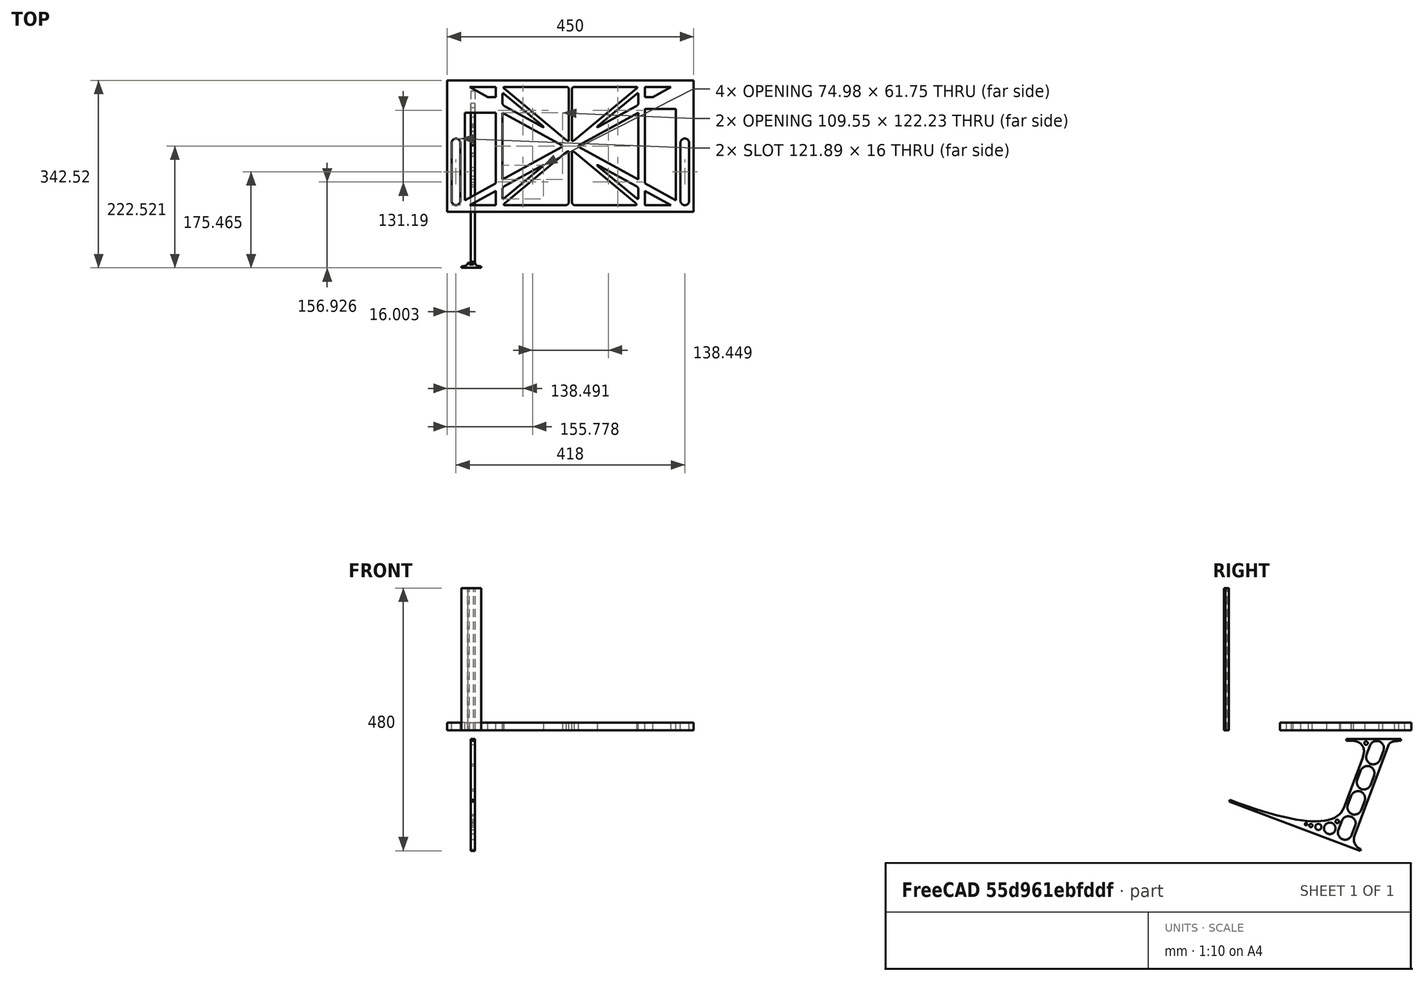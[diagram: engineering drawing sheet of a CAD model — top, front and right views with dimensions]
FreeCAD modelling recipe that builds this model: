
FCSTD DOCUMENT  (FreeCAD 0.19R0.19.2)
Label: laptopStand085
License: All rights reserved
LicenseURL: http://en.wikipedia.org/wiki/All_rights_reserved
objects: Sketcher::SketchObject×3, Part::Extrusion×3
note: 6 computed .brp shape members not serialized (recipe doc carries the construction recipe); baked Part::Feature solids carry a one-line shape summary decoded from their .brp

FEATURE [Sketcher::SketchObject] Sketch
  FullyConstrained = true
  sketch-geometry (220):
    g0: LineSegment StartX=-10.9272 StartY=-82.7794 StartZ=0 EndX=46.0728 EndY=-51.4823 EndZ=0
    g1: LineSegment StartX=366.073 StartY=-91.7794 StartZ=0 EndX=318.073 EndY=-65.424 EndZ=0
    g2: LineSegment StartX=-10.9272 StartY=77.3346 StartZ=0 EndX=-10.9272 EndY=-82.7794 EndZ=0
    g3: LineSegment StartX=375.073 StartY=-82.7794 StartZ=0 EndX=375.073 EndY=83.9235 EndZ=0
    g4: LineSegment StartX=-1.92719 StartY=-91.7794 StartZ=0 EndX=46.0728 EndY=-91.7794 EndZ=0
    g5: LineSegment StartX=318.073 StartY=124.221 StartZ=0 EndX=366.073 EndY=124.221 EndZ=0
    g6: LineSegment StartX=306.073 StartY=77.3346 StartZ=0 EndX=306.073 EndY=-44.8935 EndZ=0
    g7: LineSegment StartX=318.073 StartY=83.9235 StartZ=0 EndX=318.073 EndY=-51.4823 EndZ=0
    g8: LineSegment StartX=318.073 StartY=-51.4823 StartZ=0 EndX=375.073 EndY=-82.7794 EndZ=0
    g9: LineSegment StartX=318.073 StartY=-65.424 StartZ=0 EndX=318.073 EndY=-91.7794 EndZ=0
    g10: LineSegment StartX=318.073 StartY=-91.7794 StartZ=0 EndX=366.073 EndY=-91.7794 EndZ=0
    g11: LineSegment StartX=58.0728 StartY=-44.8935 StartZ=0 EndX=58.0728 EndY=77.3346 EndZ=0
    g12: LineSegment StartX=46.0728 StartY=-65.424 StartZ=0 EndX=-1.92719 EndY=-91.7794 EndZ=0
    g13: LineSegment StartX=46.0728 StartY=-65.424 StartZ=0 EndX=46.0728 EndY=-91.7794 EndZ=0
    g14: LineSegment StartX=46.0728 StartY=77.3346 StartZ=0 EndX=46.0728 EndY=-51.4823 EndZ=0
    g15: LineSegment StartX=-42.9272 StartY=136.221 StartZ=0 EndX=-42.9272 EndY=-103.779 EndZ=0
    g16: LineSegment StartX=407.073 StartY=136.221 StartZ=0 EndX=407.073 EndY=-103.779 EndZ=0
    g17: ArcOfCircle CenterX=-26.9272 CenterY=22.1087 CenterZ=0 NormalX=0 NormalY=0 NormalZ=1 AngleXU=0 Radius=8 StartAngle=1e-16 EndAngle=3.14159
    g18: ArcOfCircle CenterX=-26.9272 CenterY=-83.7794 CenterZ=0 NormalX=0 NormalY=0 NormalZ=1 AngleXU=0 Radius=8 StartAngle=3.14159 EndAngle=6.28319
    g19: LineSegment StartX=-34.9272 StartY=22.1087 StartZ=0 EndX=-34.9272 EndY=-83.7794 EndZ=0
    g20: LineSegment StartX=-18.9272 StartY=22.1087 StartZ=0 EndX=-18.9272 EndY=-83.7794 EndZ=0
    g21: ArcOfCircle CenterX=391.073 CenterY=22.1087 CenterZ=0 NormalX=0 NormalY=0 NormalZ=1 AngleXU=0 Radius=8 StartAngle=-4.4e-15 EndAngle=3.14159
    g22: LineSegment StartX=399.073 StartY=22.1087 StartZ=0 EndX=399.073 EndY=-83.7794 EndZ=0
    g23: LineSegment StartX=383.073 StartY=22.1087 StartZ=0 EndX=383.073 EndY=-83.7794 EndZ=0
    g24: ArcOfCircle CenterX=391.073 CenterY=-83.7794 CenterZ=0 NormalX=0 NormalY=0 NormalZ=1 AngleXU=0 Radius=8 StartAngle=3.14159 EndAngle=6.28319
    g25: Circle CenterX=175.022 CenterY=27.0628 CenterZ=0 NormalX=0 NormalY=0 NormalZ=1 AngleXU=0 Radius=1
    g26: Circle CenterX=179.022 CenterY=24.8665 CenterZ=0 NormalX=0 NormalY=0 NormalZ=1 AngleXU=0 Radius=1
    g27: Circle CenterX=179.022 CenterY=27.0628 CenterZ=0 NormalX=0 NormalY=0 NormalZ=1 AngleXU=0 Radius=1
    g28: BSplineCurve PolesCount=3 KnotsCount=2 Degree=2 IsPeriodic=0
    g29: GeomPoint X=175.022 Y=27.0628 Z=0
    g30: GeomPoint X=179.022 Y=27.0628 Z=0
    g31: Circle CenterX=189.124 CenterY=27.0628 CenterZ=0 NormalX=0 NormalY=0 NormalZ=1 AngleXU=0 Radius=1
    g32: Circle CenterX=185.124 CenterY=24.8665 CenterZ=0 NormalX=0 NormalY=0 NormalZ=1 AngleXU=0 Radius=1
    g33: Circle CenterX=185.124 CenterY=27.0628 CenterZ=0 NormalX=0 NormalY=0 NormalZ=1 AngleXU=0 Radius=1
    g34: BSplineCurve PolesCount=3 KnotsCount=2 Degree=2 IsPeriodic=0
    g35: GeomPoint X=189.124 Y=27.0628 Z=0
    g36: GeomPoint X=185.124 Y=27.0628 Z=0
    g37: Circle CenterX=175.022 CenterY=5.37834 CenterZ=0 NormalX=0 NormalY=0 NormalZ=1 AngleXU=0 Radius=1
    g38: Circle CenterX=179.022 CenterY=7.57463 CenterZ=0 NormalX=0 NormalY=0 NormalZ=1 AngleXU=0 Radius=1
    g39: Circle CenterX=179.022 CenterY=5.34704 CenterZ=0 NormalX=0 NormalY=0 NormalZ=1 AngleXU=0 Radius=1
    g40: BSplineCurve PolesCount=3 KnotsCount=2 Degree=2 IsPeriodic=0
    g41: GeomPoint X=175.022 Y=5.37834 Z=0
    g42: GeomPoint X=179.022 Y=5.34704 Z=0
    g43: Circle CenterX=189.124 CenterY=5.37834 CenterZ=0 NormalX=0 NormalY=0 NormalZ=1 AngleXU=0 Radius=1
    g44: Circle CenterX=185.124 CenterY=7.57463 CenterZ=0 NormalX=0 NormalY=0 NormalZ=1 AngleXU=0 Radius=1
    g45: Circle CenterX=185.124 CenterY=5.34704 CenterZ=0 NormalX=0 NormalY=0 NormalZ=1 AngleXU=0 Radius=1
    g46: BSplineCurve PolesCount=3 KnotsCount=2 Degree=2 IsPeriodic=0
    g47: GeomPoint X=189.124 Y=5.37834 Z=0
    g48: GeomPoint X=185.124 Y=5.34704 Z=0
    g49: Circle CenterX=165.871 CenterY=18.1458 CenterZ=0 NormalX=0 NormalY=0 NormalZ=1 AngleXU=0 Radius=1
    g50: Circle CenterX=169.377 CenterY=16.2206 CenterZ=0 NormalX=0 NormalY=0 NormalZ=1 AngleXU=0 Radius=1
    g51: Circle CenterX=165.871 CenterY=14.2954 CenterZ=0 NormalX=0 NormalY=0 NormalZ=1 AngleXU=0 Radius=1
    g52: BSplineCurve PolesCount=3 KnotsCount=2 Degree=2 IsPeriodic=0
    g53: GeomPoint X=165.871 Y=18.1458 Z=0
    g54: GeomPoint X=165.871 Y=14.2954 Z=0
    g55: Circle CenterX=198.275 CenterY=18.1458 CenterZ=0 NormalX=0 NormalY=0 NormalZ=1 AngleXU=0 Radius=1
    g56: Circle CenterX=194.768 CenterY=16.2206 CenterZ=0 NormalX=0 NormalY=0 NormalZ=1 AngleXU=0 Radius=1
    g57: Circle CenterX=198.275 CenterY=14.2954 CenterZ=0 NormalX=0 NormalY=0 NormalZ=1 AngleXU=0 Radius=1
    g58: BSplineCurve PolesCount=3 KnotsCount=2 Degree=2 IsPeriodic=0
    g59: GeomPoint X=198.275 Y=18.1458 Z=0
    g60: GeomPoint X=198.275 Y=14.2954 Z=0
    g61: LineSegment StartX=165.871 StartY=18.1458 StartZ=0 EndX=58.0728 EndY=77.3346 EndZ=0
    g62: LineSegment StartX=58.0728 StartY=-44.8935 StartZ=0 EndX=165.871 EndY=14.2954 EndZ=0
    g63: LineSegment StartX=198.275 StartY=18.1458 StartZ=0 EndX=306.073 EndY=77.3346 EndZ=0
    g64: LineSegment StartX=198.275 StartY=14.2954 StartZ=0 EndX=306.073 EndY=-44.8935 EndZ=0
    g65: LineSegment StartX=407.073 StartY=-103.779 StartZ=0 EndX=-42.9272 EndY=-103.779 EndZ=0
    g66: LineSegment StartX=407.073 StartY=136.221 StartZ=0 EndX=-42.9272 EndY=136.221 EndZ=0
    g67: LineSegment StartX=46.0728 StartY=77.3346 StartZ=0 EndX=-10.9272 EndY=77.3346 EndZ=0
    g68: LineSegment StartX=46.0728 StartY=105.865 StartZ=0 EndX=31.5028 EndY=105.865 EndZ=0
    g69: LineSegment StartX=46.0728 StartY=124.221 StartZ=0 EndX=46.0728 EndY=105.865 EndZ=0
    g70: LineSegment StartX=-1.92719 StartY=124.221 StartZ=0 EndX=31.5028 EndY=105.865 EndZ=0
    g71: LineSegment StartX=46.0728 StartY=124.221 StartZ=0 EndX=-1.92719 EndY=124.221 EndZ=0
    g72: LineSegment StartX=318.073 StartY=83.9235 StartZ=0 EndX=375.073 EndY=83.9235 EndZ=0
    g73: LineSegment StartX=318.073 StartY=105.865 StartZ=0 EndX=332.643 EndY=105.865 EndZ=0
    g74: LineSegment StartX=332.643 StartY=105.865 StartZ=0 EndX=366.073 EndY=124.221 EndZ=0
    g75: LineSegment StartX=318.073 StartY=124.221 StartZ=0 EndX=318.073 EndY=105.865 EndZ=0
    g76: Circle CenterX=125.607 CenterY=54.1951 CenterZ=0 NormalX=0 NormalY=0 NormalZ=1 AngleXU=0 Radius=1
    g77: Circle CenterX=139.632 CenterY=46.4944 CenterZ=0 NormalX=0 NormalY=0 NormalZ=1 AngleXU=0 Radius=1
    g78: Circle CenterX=127.326 CenterY=56.7187 CenterZ=0 NormalX=0 NormalY=0 NormalZ=1 AngleXU=0 Radius=1
    g79: BSplineCurve PolesCount=3 KnotsCount=2 Degree=2 IsPeriodic=0
    g80: GeomPoint X=125.607 Y=54.1951 Z=0
    g81: GeomPoint X=127.326 Y=56.7187 Z=0
    g82: Circle CenterX=236.821 CenterY=56.7187 CenterZ=0 NormalX=0 NormalY=0 NormalZ=1 AngleXU=0 Radius=1
    g83: Circle CenterX=224.513 CenterY=46.4944 CenterZ=0 NormalX=0 NormalY=0 NormalZ=1 AngleXU=0 Radius=1
    g84: Circle CenterX=238.538 CenterY=54.1951 CenterZ=0 NormalX=0 NormalY=0 NormalZ=1 AngleXU=0 Radius=1
    g85: BSplineCurve PolesCount=3 KnotsCount=2 Degree=2 IsPeriodic=0
    g86: GeomPoint X=236.821 Y=56.7187 Z=0
    g87: GeomPoint X=238.538 Y=54.1951 Z=0
    g88: Circle CenterX=238.538 CenterY=-21.7539 CenterZ=0 NormalX=0 NormalY=0 NormalZ=1 AngleXU=0 Radius=1
    g89: Circle CenterX=224.513 CenterY=-14.0532 CenterZ=0 NormalX=0 NormalY=0 NormalZ=1 AngleXU=0 Radius=1
    g90: Circle CenterX=236.821 CenterY=-24.2775 CenterZ=0 NormalX=0 NormalY=0 NormalZ=1 AngleXU=0 Radius=1
    g91: BSplineCurve PolesCount=3 KnotsCount=2 Degree=2 IsPeriodic=0
    g92: GeomPoint X=238.538 Y=-21.7539 Z=0
    g93: GeomPoint X=236.821 Y=-24.2775 Z=0
    g94: Circle CenterX=125.607 CenterY=-21.7539 CenterZ=0 NormalX=0 NormalY=0 NormalZ=1 AngleXU=0 Radius=1
    g95: Circle CenterX=139.632 CenterY=-14.0532 CenterZ=0 NormalX=0 NormalY=0 NormalZ=1 AngleXU=0 Radius=1
    g96: Circle CenterX=127.325 CenterY=-24.2775 CenterZ=0 NormalX=0 NormalY=0 NormalZ=1 AngleXU=0 Radius=1
    g97: BSplineCurve PolesCount=3 KnotsCount=2 Degree=2 IsPeriodic=0
    g98: GeomPoint X=125.607 Y=-21.7539 Z=0
    g99: GeomPoint X=127.325 Y=-24.2775 Z=0
    g100: Circle CenterX=302.996 CenterY=111.695 CenterZ=0 NormalX=0 NormalY=0 NormalZ=1 AngleXU=0 Radius=1
    g101: Circle CenterX=306.073 CenterY=114.251 CenterZ=0 NormalX=0 NormalY=0 NormalZ=1 AngleXU=0 Radius=1
    g102: Circle CenterX=306.073 CenterY=110.251 CenterZ=0 NormalX=0 NormalY=0 NormalZ=1 AngleXU=0 Radius=1
    g103: BSplineCurve PolesCount=3 KnotsCount=2 Degree=2 IsPeriodic=0
    g104: GeomPoint X=302.996 Y=111.695 Z=0
    g105: GeomPoint X=306.073 Y=110.251 Z=0
    g106: Circle CenterX=306.073 CenterY=95.2763 CenterZ=0 NormalX=0 NormalY=0 NormalZ=1 AngleXU=0 Radius=1
    g107: Circle CenterX=306.073 CenterY=91.2763 CenterZ=0 NormalX=0 NormalY=0 NormalZ=1 AngleXU=0 Radius=1
    g108: Circle CenterX=302.567 CenterY=89.3511 CenterZ=0 NormalX=0 NormalY=0 NormalZ=1 AngleXU=0 Radius=1
    g109: BSplineCurve PolesCount=3 KnotsCount=2 Degree=2 IsPeriodic=0
    g110: GeomPoint X=306.073 Y=95.2763 Z=0
    g111: GeomPoint X=302.567 Y=89.3511 Z=0
    g112: LineSegment StartX=306.073 StartY=110.251 StartZ=0 EndX=306.073 EndY=95.2763 EndZ=0
    g113: LineSegment StartX=302.996 StartY=111.695 StartZ=0 EndX=236.821 EndY=56.7187 EndZ=0
    g114: LineSegment StartX=238.538 StartY=54.1951 StartZ=0 EndX=302.567 EndY=89.3511 EndZ=0
    g115: Circle CenterX=61.1496 CenterY=111.695 CenterZ=0 NormalX=0 NormalY=0 NormalZ=1 AngleXU=0 Radius=1
    g116: Circle CenterX=58.0728 CenterY=114.251 CenterZ=0 NormalX=0 NormalY=0 NormalZ=1 AngleXU=0 Radius=1
    g117: Circle CenterX=58.0728 CenterY=110.251 CenterZ=0 NormalX=0 NormalY=0 NormalZ=1 AngleXU=0 Radius=1
    g118: BSplineCurve PolesCount=3 KnotsCount=2 Degree=2 IsPeriodic=0
    g119: GeomPoint X=61.1496 Y=111.695 Z=0
    g120: GeomPoint X=58.0728 Y=110.251 Z=0
    g121: Circle CenterX=61.5791 CenterY=89.3511 CenterZ=0 NormalX=0 NormalY=0 NormalZ=1 AngleXU=0 Radius=1
    g122: Circle CenterX=58.0728 CenterY=91.2763 CenterZ=0 NormalX=0 NormalY=0 NormalZ=1 AngleXU=0 Radius=1
    g123: Circle CenterX=58.0728 CenterY=95.2763 CenterZ=0 NormalX=0 NormalY=0 NormalZ=1 AngleXU=0 Radius=1
    g124: BSplineCurve PolesCount=3 KnotsCount=2 Degree=2 IsPeriodic=0
    g125: GeomPoint X=61.5791 Y=89.3511 Z=0
    g126: GeomPoint X=58.0728 Y=95.2763 Z=0
    g127: LineSegment StartX=58.0728 StartY=110.251 StartZ=0 EndX=58.0728 EndY=95.2763 EndZ=0
    g128: LineSegment StartX=61.1496 StartY=111.695 StartZ=0 EndX=127.326 EndY=56.7187 EndZ=0
    g129: LineSegment StartX=125.607 StartY=54.1951 StartZ=0 EndX=61.5791 EndY=89.3511 EndZ=0
    g130: Circle CenterX=61.5791 CenterY=-56.9099 CenterZ=0 NormalX=0 NormalY=0 NormalZ=1 AngleXU=0 Radius=1
    g131: Circle CenterX=58.0728 CenterY=-58.8351 CenterZ=0 NormalX=0 NormalY=0 NormalZ=1 AngleXU=0 Radius=1
    g132: Circle CenterX=58.0728 CenterY=-62.8351 CenterZ=0 NormalX=0 NormalY=0 NormalZ=1 AngleXU=0 Radius=1
    g133: BSplineCurve PolesCount=3 KnotsCount=2 Degree=2 IsPeriodic=0
    g134: GeomPoint X=61.5791 Y=-56.9099 Z=0
    g135: GeomPoint X=58.0728 Y=-62.8351 Z=0
    g136: Circle CenterX=58.0728 CenterY=-77.8102 CenterZ=0 NormalX=0 NormalY=0 NormalZ=1 AngleXU=0 Radius=1
    g137: Circle CenterX=58.0728 CenterY=-81.8102 CenterZ=0 NormalX=0 NormalY=0 NormalZ=1 AngleXU=0 Radius=1
    g138: Circle CenterX=61.1496 CenterY=-79.2541 CenterZ=0 NormalX=0 NormalY=0 NormalZ=1 AngleXU=0 Radius=1
    g139: BSplineCurve PolesCount=3 KnotsCount=2 Degree=2 IsPeriodic=0
    g140: GeomPoint X=58.0728 Y=-77.8102 Z=0
    g141: GeomPoint X=61.1496 Y=-79.2541 Z=0
    g142: LineSegment StartX=58.0728 StartY=-62.8351 StartZ=0 EndX=58.0728 EndY=-77.8102 EndZ=0
    g143: LineSegment StartX=61.1496 StartY=-79.2541 StartZ=0 EndX=127.325 EndY=-24.2775 EndZ=0
    g144: LineSegment StartX=125.607 StartY=-21.7539 StartZ=0 EndX=61.5791 EndY=-56.9099 EndZ=0
    g145: Circle CenterX=302.567 CenterY=-56.9099 CenterZ=0 NormalX=0 NormalY=0 NormalZ=1 AngleXU=0 Radius=1
    g146: Circle CenterX=306.073 CenterY=-58.8351 CenterZ=0 NormalX=0 NormalY=0 NormalZ=1 AngleXU=0 Radius=1
    g147: Circle CenterX=306.073 CenterY=-62.8351 CenterZ=0 NormalX=0 NormalY=0 NormalZ=1 AngleXU=0 Radius=1
    g148: BSplineCurve PolesCount=3 KnotsCount=2 Degree=2 IsPeriodic=0
    g149: GeomPoint X=302.567 Y=-56.9099 Z=0
    g150: GeomPoint X=306.073 Y=-62.8351 Z=0
    g151: Circle CenterX=302.996 CenterY=-79.2541 CenterZ=0 NormalX=0 NormalY=0 NormalZ=1 AngleXU=0 Radius=1
    g152: Circle CenterX=306.073 CenterY=-81.8102 CenterZ=0 NormalX=0 NormalY=0 NormalZ=1 AngleXU=0 Radius=1
    g153: Circle CenterX=306.073 CenterY=-77.8102 CenterZ=0 NormalX=0 NormalY=0 NormalZ=1 AngleXU=0 Radius=1
    g154: BSplineCurve PolesCount=3 KnotsCount=2 Degree=2 IsPeriodic=0
    g155: GeomPoint X=302.996 Y=-79.2541 Z=0
    g156: GeomPoint X=306.073 Y=-77.8102 Z=0
    g157: LineSegment StartX=306.073 StartY=-62.8351 StartZ=0 EndX=306.073 EndY=-77.8102 EndZ=0
    g158: LineSegment StartX=302.996 StartY=-79.2541 StartZ=0 EndX=236.821 EndY=-24.2775 EndZ=0
    g159: LineSegment StartX=238.538 StartY=-21.7539 StartZ=0 EndX=302.567 EndY=-56.9099 EndZ=0
    g160: Circle CenterX=61.6457 CenterY=-88.8112 CenterZ=0 NormalX=0 NormalY=0 NormalZ=1 AngleXU=0 Radius=1
    g161: Circle CenterX=58.0728 CenterY=-91.7794 CenterZ=0 NormalX=0 NormalY=0 NormalZ=1 AngleXU=0 Radius=1
    g162: Circle CenterX=63.9135 CenterY=-91.7794 CenterZ=0 NormalX=0 NormalY=0 NormalZ=1 AngleXU=0 Radius=1
    g163: BSplineCurve PolesCount=3 KnotsCount=2 Degree=2 IsPeriodic=0
    g164: GeomPoint X=61.6457 Y=-88.8112 Z=0
    g165: GeomPoint X=63.9135 Y=-91.7794 Z=0
    g166: Circle CenterX=179.022 CenterY=-85.8163 CenterZ=0 NormalX=0 NormalY=0 NormalZ=1 AngleXU=0 Radius=1
    g167: Circle CenterX=179.022 CenterY=-91.7794 CenterZ=0 NormalX=0 NormalY=0 NormalZ=1 AngleXU=0 Radius=1
    g168: Circle CenterX=171.895 CenterY=-91.7794 CenterZ=0 NormalX=0 NormalY=0 NormalZ=1 AngleXU=0 Radius=1
    g169: BSplineCurve PolesCount=3 KnotsCount=2 Degree=2 IsPeriodic=0
    g170: GeomPoint X=179.022 Y=-85.8163 Z=0
    g171: GeomPoint X=171.895 Y=-91.7794 Z=0
    g172: Circle CenterX=185.124 CenterY=-86.2028 CenterZ=0 NormalX=0 NormalY=0 NormalZ=1 AngleXU=0 Radius=1
    g173: Circle CenterX=185.124 CenterY=-91.7794 CenterZ=0 NormalX=0 NormalY=0 NormalZ=1 AngleXU=0 Radius=1
    g174: Circle CenterX=191.747 CenterY=-91.7794 CenterZ=0 NormalX=0 NormalY=0 NormalZ=1 AngleXU=0 Radius=1
    g175: BSplineCurve PolesCount=3 KnotsCount=2 Degree=2 IsPeriodic=0
    g176: GeomPoint X=185.124 Y=-86.2028 Z=0
    g177: GeomPoint X=191.747 Y=-91.7794 Z=0
    g178: Circle CenterX=299.888 CenterY=-86.6413 CenterZ=0 NormalX=0 NormalY=0 NormalZ=1 AngleXU=0 Radius=1
    g179: Circle CenterX=306.073 CenterY=-91.7794 CenterZ=0 NormalX=0 NormalY=0 NormalZ=1 AngleXU=0 Radius=1
    g180: Circle CenterX=298.776 CenterY=-91.7794 CenterZ=0 NormalX=0 NormalY=0 NormalZ=1 AngleXU=0 Radius=1
    g181: BSplineCurve PolesCount=3 KnotsCount=2 Degree=2 IsPeriodic=0
    g182: GeomPoint X=299.888 Y=-86.6413 Z=0
    g183: GeomPoint X=298.776 Y=-91.7794 Z=0
    g184: LineSegment StartX=189.124 StartY=5.37834 StartZ=0 EndX=299.888 EndY=-86.6413 EndZ=0
    g185: LineSegment StartX=298.776 StartY=-91.7794 StartZ=0 EndX=191.747 EndY=-91.7794 EndZ=0
    g186: LineSegment StartX=185.124 StartY=-86.2028 StartZ=0 EndX=185.124 EndY=5.34704 EndZ=0
    g187: LineSegment StartX=179.022 StartY=5.34704 StartZ=0 EndX=179.022 EndY=-85.8163 EndZ=0
    g188: LineSegment StartX=171.895 StartY=-91.7794 StartZ=0 EndX=63.9135 EndY=-91.7794 EndZ=0
    g189: LineSegment StartX=61.6457 StartY=-88.8112 StartZ=0 EndX=175.022 EndY=5.37834 EndZ=0
    g190: Circle CenterX=302.073 CenterY=124.221 CenterZ=0 NormalX=0 NormalY=0 NormalZ=1 AngleXU=0 Radius=1
    g191: Circle CenterX=306.073 CenterY=124.221 CenterZ=0 NormalX=0 NormalY=0 NormalZ=1 AngleXU=0 Radius=1
    g192: Circle CenterX=302.996 CenterY=121.665 CenterZ=0 NormalX=0 NormalY=0 NormalZ=1 AngleXU=0 Radius=1
    g193: BSplineCurve PolesCount=3 KnotsCount=2 Degree=2 IsPeriodic=0
    g194: GeomPoint X=302.073 Y=124.221 Z=0
    g195: GeomPoint X=302.996 Y=121.665 Z=0
    g196: Circle CenterX=189.124 CenterY=124.221 CenterZ=0 NormalX=0 NormalY=0 NormalZ=1 AngleXU=0 Radius=1
    g197: Circle CenterX=185.124 CenterY=124.221 CenterZ=0 NormalX=0 NormalY=0 NormalZ=1 AngleXU=0 Radius=1
    g198: Circle CenterX=185.124 CenterY=120.221 CenterZ=0 NormalX=0 NormalY=0 NormalZ=1 AngleXU=0 Radius=1
    g199: BSplineCurve PolesCount=3 KnotsCount=2 Degree=2 IsPeriodic=0
    g200: GeomPoint X=189.124 Y=124.221 Z=0
    g201: GeomPoint X=185.124 Y=120.221 Z=0
    g202: Circle CenterX=175.022 CenterY=124.221 CenterZ=0 NormalX=0 NormalY=0 NormalZ=1 AngleXU=0 Radius=1
    g203: Circle CenterX=179.022 CenterY=124.221 CenterZ=0 NormalX=0 NormalY=0 NormalZ=1 AngleXU=0 Radius=1
    g204: Circle CenterX=179.022 CenterY=120.221 CenterZ=0 NormalX=0 NormalY=0 NormalZ=1 AngleXU=0 Radius=1
    g205: BSplineCurve PolesCount=3 KnotsCount=2 Degree=2 IsPeriodic=0
    g206: GeomPoint X=175.022 Y=124.221 Z=0
    g207: GeomPoint X=179.022 Y=120.221 Z=0
    g208: Circle CenterX=62.0728 CenterY=124.221 CenterZ=0 NormalX=0 NormalY=0 NormalZ=1 AngleXU=0 Radius=1
    g209: Circle CenterX=58.0728 CenterY=124.221 CenterZ=0 NormalX=0 NormalY=0 NormalZ=1 AngleXU=0 Radius=1
    g210: Circle CenterX=61.1496 CenterY=121.665 CenterZ=0 NormalX=0 NormalY=0 NormalZ=1 AngleXU=0 Radius=1
    g211: BSplineCurve PolesCount=3 KnotsCount=2 Degree=2 IsPeriodic=0
    g212: GeomPoint X=62.0728 Y=124.221 Z=0
    g213: GeomPoint X=61.1496 Y=121.665 Z=0
    g214: LineSegment StartX=62.0728 StartY=124.221 StartZ=0 EndX=175.022 EndY=124.221 EndZ=0
    g215: LineSegment StartX=179.022 StartY=120.221 StartZ=0 EndX=179.022 EndY=27.0628 EndZ=0
    g216: LineSegment StartX=185.124 StartY=27.0628 StartZ=0 EndX=185.124 EndY=120.221 EndZ=0
    g217: LineSegment StartX=189.124 StartY=124.221 StartZ=0 EndX=302.073 EndY=124.221 EndZ=0
    g218: LineSegment StartX=302.996 StartY=121.665 StartZ=0 EndX=189.124 EndY=27.0628 EndZ=0
    g219: LineSegment StartX=175.022 StartY=27.0628 StartZ=0 EndX=61.1496 EndY=121.665 EndZ=0
  constraints (375):
    c: Horizontal(g4)
    c: Horizontal(g5)
    c: Coincident(g7,g8)
    c: Coincident(g9,g1)
    c: Tangent(g7,g9)
    c: Coincident(g13,g12)
    c: Coincident(g0,g14)
    c: Block(g8)
    c: Block(g3)
    c: Block(g1)
    c: Block(g9)
    c: Block(g13)
    c: Block(g12)
    c: Block(g0)
    c: Block(g2)
    c: Block(g6)
    c: Block(g5)
    c: Block(g10)
    c: Block(g4)
    c: Vertical(g15)
    c: Vertical(g16)
    c: Block(g16)
    c: Block(g15)
    c: Tangent(g17,g20) = 1.5708
    c: Tangent(g17,g19) = -1.5708
    c: Tangent(g19,g18) = -1.5708
    c: Tangent(g20,g18) = 1.5708
    c: Vertical(g19)
    c: Equal(g17,g18)
    c: Block(g20)
    c: Block(g19)
    c: Tangent(g21,g22) = 1.5708
    c: Tangent(g22,g24) = 1.5708
    c: Equal(g21,g24)
    c: Coincident(g23,g21)
    c: Coincident(g23,g24)
    c: Block(g22)
    c: Block(g23)
    c: Weight(g25) = 1
    c: Equal(g25,g26)
    c: Equal(g25,g27)
    c: InternalAlignment(g25,g28)
    c: InternalAlignment(g26,g28)
    c: InternalAlignment(g27,g28)
    c: InternalAlignment(g29,g28)
    c: InternalAlignment(g30,g28)
    c: Weight(g31) = 1
    c: Equal(g31,g32)
    c: Equal(g31,g33)
    c: InternalAlignment(g31,g34)
    c: InternalAlignment(g32,g34)
    c: InternalAlignment(g33,g34)
    c: InternalAlignment(g35,g34)
    c: InternalAlignment(g36,g34)
    c: Block(g34)
    c: Block(g28)
    c: Weight(g37) = 1
    c: Equal(g37,g38)
    c: Equal(g37,g39)
    c: InternalAlignment(g37,g40)
    c: InternalAlignment(g38,g40)
    c: InternalAlignment(g39,g40)
    c: InternalAlignment(g41,g40)
    c: InternalAlignment(g42,g40)
    c: Weight(g43) = 1
    c: Equal(g43,g44)
    c: Equal(g43,g45)
    c: InternalAlignment(g43,g46)
    c: InternalAlignment(g44,g46)
    c: InternalAlignment(g45,g46)
    c: InternalAlignment(g47,g46)
    c: InternalAlignment(g48,g46)
    c: Block(g46)
    c: Block(g40)
    c: Weight(g49) = 1
    c: Equal(g49,g50)
    c: Equal(g49,g51)
    c: InternalAlignment(g49,g52)
    c: InternalAlignment(g50,g52)
    c: InternalAlignment(g51,g52)
    c: InternalAlignment(g53,g52)
    c: InternalAlignment(g54,g52)
    c: Weight(g55) = 1
    c: Equal(g55,g56)
    c: Equal(g55,g57)
    c: InternalAlignment(g55,g58)
    c: InternalAlignment(g56,g58)
    c: InternalAlignment(g57,g58)
    c: InternalAlignment(g59,g58)
    c: InternalAlignment(g60,g58)
    c: Block(g52)
    c: Block(g58)
    c: Coincident(g61,g52)
    c: Coincident(g61,g11)
    c: Coincident(g62,g11)
    c: Coincident(g62,g52)
    c: Coincident(g63,g58)
    c: Coincident(g63,g6)
    c: Coincident(g64,g58)
    c: Coincident(g64,g6)
    c: Block(g11)
    c: Coincident(g65,g16)
    c: Coincident(g65,g15)
    c: Horizontal(g65)
    c: Distance(g65) = 450
    c: Coincident(g66,g16)
    c: Coincident(g66,g15)
    c: Horizontal(g66)
    c: Horizontal(g67)
    c: Coincident(g14,g67)
    c: Horizontal(g68)
    c: Vertical(g69)
    c: Block(g69)
    c: Block(g68)
    c: Block(g67)
    c: Distance(g69) = 18.3554
    c: Coincident(g71,g69)
    c: Coincident(g71,g70)
    c: Horizontal(g71)
    c: Block(g71)
    c: Block(g70)
    c: Coincident(g68,g70)
    c: Coincident(g2,g67)
    c: Coincident(g72,g7)
    c: Horizontal(g72)
    c: Horizontal(g73)
    c: Block(g72)
    c: Coincident(g74,g5)
    c: Coincident(g75,g5)
    c: Coincident(g75,g73)
    c: Vertical(g75)
    c: Block(g75)
    c: Coincident(g73,g74)
    c: Block(g74)
    c: Coincident(g3,g72)
    c: Weight(g76) = 1
    c: Equal(g76,g77)
    c: Equal(g76,g78)
    c: InternalAlignment(g76,g79)
    c: InternalAlignment(g77,g79)
    c: InternalAlignment(g78,g79)
    c: InternalAlignment(g80,g79)
    c: InternalAlignment(g81,g79)
    c: Block(g79)
    c: Weight(g82) = 1
    c: Equal(g82,g83)
    c: Equal(g82,g84)
    c: InternalAlignment(g82,g85)
    c: InternalAlignment(g83,g85)
    c: InternalAlignment(g84,g85)
    c: InternalAlignment(g86,g85)
    c: InternalAlignment(g87,g85)
    c: Block(g85)
    c: Weight(g88) = 1
    c: Equal(g88,g89)
    c: Equal(g88,g90)
    c: InternalAlignment(g88,g91)
    c: InternalAlignment(g89,g91)
    c: InternalAlignment(g90,g91)
    c: InternalAlignment(g92,g91)
    c: InternalAlignment(g93,g91)
    c: Block(g91)
    c: Weight(g94) = 1
    c: Equal(g94,g95)
    c: Equal(g94,g96)
    c: InternalAlignment(g94,g97)
    c: InternalAlignment(g95,g97)
    c: InternalAlignment(g96,g97)
    c: InternalAlignment(g98,g97)
    c: InternalAlignment(g99,g97)
    c: Block(g97)
    c: Weight(g100) = 1
    c: Equal(g100,g101)
    c: Equal(g100,g102)
    c: InternalAlignment(g100,g103)
    c: InternalAlignment(g101,g103)
    c: InternalAlignment(g102,g103)
    c: InternalAlignment(g104,g103)
    c: InternalAlignment(g105,g103)
    c: Weight(g106) = 1
    c: Equal(g106,g107)
    c: Equal(g106,g108)
    c: InternalAlignment(g106,g109)
    c: InternalAlignment(g107,g109)
    c: InternalAlignment(g108,g109)
    c: InternalAlignment(g110,g109)
    c: InternalAlignment(g111,g109)
    c: Block(g103)
    c: Block(g109)
    c: Coincident(g112,g103)
    c: Coincident(g112,g109)
    c: Vertical(g112)
    c: Coincident(g113,g103)
    c: Coincident(g113,g85)
    c: Coincident(g114,g85)
    c: Coincident(g114,g109)
    c: Weight(g115) = 1
    c: Equal(g115,g116)
    c: Equal(g115,g117)
    c: InternalAlignment(g115,g118)
    c: InternalAlignment(g116,g118)
    c: InternalAlignment(g117,g118)
    c: InternalAlignment(g119,g118)
    c: InternalAlignment(g120,g118)
    c: Weight(g121) = 1
    c: Equal(g121,g122)
    c: Equal(g121,g123)
    c: InternalAlignment(g121,g124)
    c: InternalAlignment(g122,g124)
    c: InternalAlignment(g123,g124)
    c: InternalAlignment(g125,g124)
    c: InternalAlignment(g126,g124)
    c: Block(g118)
    c: Block(g124)
    c: Coincident(g127,g118)
    c: Coincident(g127,g124)
    c: Vertical(g127)
    c: Coincident(g128,g118)
    c: Coincident(g128,g79)
    c: Coincident(g129,g79)
    c: Coincident(g129,g124)
    c: Weight(g130) = 1
    c: Equal(g130,g131)
    c: Equal(g130,g132)
    c: InternalAlignment(g130,g133)
    c: InternalAlignment(g131,g133)
    c: InternalAlignment(g132,g133)
    c: InternalAlignment(g134,g133)
    c: InternalAlignment(g135,g133)
    c: Weight(g136) = 1
    c: Equal(g136,g137)
    c: Equal(g136,g138)
    c: InternalAlignment(g136,g139)
    c: InternalAlignment(g137,g139)
    c: InternalAlignment(g138,g139)
    c: InternalAlignment(g140,g139)
    c: InternalAlignment(g141,g139)
    c: Block(g133)
    c: Block(g139)
    c: Coincident(g142,g133)
    c: Coincident(g142,g139)
    c: Vertical(g142)
    c: Coincident(g143,g139)
    c: Coincident(g143,g97)
    c: Coincident(g144,g97)
    c: Coincident(g144,g133)
    c: Weight(g145) = 1
    c: Equal(g145,g146)
    c: Equal(g145,g147)
    c: InternalAlignment(g145,g148)
    c: InternalAlignment(g146,g148)
    c: InternalAlignment(g147,g148)
    c: InternalAlignment(g149,g148)
    c: InternalAlignment(g150,g148)
    c: Weight(g151) = 1
    c: Equal(g151,g152)
    c: Equal(g151,g153)
    c: InternalAlignment(g151,g154)
    c: InternalAlignment(g152,g154)
    c: InternalAlignment(g153,g154)
    c: InternalAlignment(g155,g154)
    c: InternalAlignment(g156,g154)
    c: Block(g148)
    c: Block(g154)
    c: Coincident(g157,g148)
    c: Coincident(g157,g154)
    c: Vertical(g157)
    c: Coincident(g158,g154)
    c: Coincident(g158,g91)
    c: Coincident(g159,g91)
    c: Coincident(g159,g148)
    c: Weight(g160) = 1
    c: Equal(g160,g161)
    c: Equal(g160,g162)
    c: InternalAlignment(g160,g163)
    c: InternalAlignment(g161,g163)
    c: InternalAlignment(g162,g163)
    c: InternalAlignment(g164,g163)
    c: InternalAlignment(g165,g163)
    c: Weight(g166) = 1
    c: Equal(g166,g167)
    c: Equal(g166,g168)
    c: InternalAlignment(g166,g169)
    c: InternalAlignment(g167,g169)
    c: InternalAlignment(g168,g169)
    c: InternalAlignment(g170,g169)
    c: InternalAlignment(g171,g169)
    c: Weight(g172) = 1
    c: Equal(g172,g173)
    c: Equal(g172,g174)
    c: InternalAlignment(g172,g175)
    c: InternalAlignment(g173,g175)
    c: InternalAlignment(g174,g175)
    c: InternalAlignment(g176,g175)
    c: InternalAlignment(g177,g175)
    c: Weight(g178) = 1
    c: Equal(g178,g179)
    c: Equal(g178,g180)
    c: InternalAlignment(g178,g181)
    c: InternalAlignment(g179,g181)
    c: InternalAlignment(g180,g181)
    c: InternalAlignment(g182,g181)
    c: InternalAlignment(g183,g181)
    c: Block(g181)
    c: Block(g175)
    c: Block(g169)
    c: Block(g163)
    c: Coincident(g184,g46)
    c: Coincident(g184,g181)
    c: Coincident(g185,g181)
    c: Coincident(g185,g175)
    c: Horizontal(g185)
    c: Coincident(g186,g175)
    c: Coincident(g186,g46)
    c: Vertical(g186)
    c: Coincident(g187,g40)
    c: Coincident(g187,g169)
    c: Vertical(g187)
    c: Coincident(g188,g169)
    c: Coincident(g188,g163)
    c: Horizontal(g188)
    c: Coincident(g189,g163)
    c: Coincident(g189,g40)
    c: Weight(g190) = 1
    c: Equal(g190,g191)
    c: Equal(g190,g192)
    c: InternalAlignment(g190,g193)
    c: InternalAlignment(g191,g193)
    c: InternalAlignment(g192,g193)
    c: InternalAlignment(g194,g193)
    c: InternalAlignment(g195,g193)
    c: Weight(g196) = 1
    c: Equal(g196,g197)
    c: Equal(g196,g198)
    c: InternalAlignment(g196,g199)
    c: InternalAlignment(g197,g199)
    c: InternalAlignment(g198,g199)
    c: InternalAlignment(g200,g199)
    c: InternalAlignment(g201,g199)
    c: Weight(g202) = 1
    c: Equal(g202,g203)
    c: Equal(g202,g204)
    c: InternalAlignment(g202,g205)
    c: InternalAlignment(g203,g205)
    c: InternalAlignment(g204,g205)
    c: InternalAlignment(g206,g205)
    c: InternalAlignment(g207,g205)
    c: Weight(g208) = 1
    c: Equal(g208,g209)
    c: Equal(g208,g210)
    c: InternalAlignment(g208,g211)
    c: InternalAlignment(g209,g211)
    c: InternalAlignment(g210,g211)
    c: InternalAlignment(g212,g211)
    c: InternalAlignment(g213,g211)
    c: Block(g211)
    c: Block(g205)
    c: Block(g199)
    c: Block(g193)
    c: Coincident(g214,g211)
    c: Coincident(g214,g205)
    c: Horizontal(g214)
    c: Coincident(g215,g205)
    c: Coincident(g215,g28)
    c: Vertical(g215)
    c: Coincident(g216,g34)
    c: Coincident(g216,g199)
    c: Vertical(g216)
    c: Coincident(g217,g199)
    c: Coincident(g217,g193)
    c: Horizontal(g217)
    c: Coincident(g218,g193)
    c: Coincident(g218,g34)
    c: Coincident(g219,g28)
    c: Coincident(g219,g211)
FEATURE [Sketcher::SketchObject] Sketch001
  FullyConstrained = true
  MapMode = 4
  Placement = pos=(0,0,0) rot=(0.57735,0.57735,0.57735;2.0944rad)
  Support = -> [Sketch]
  sketch-geometry (46):
    g0: BSplineCurve PolesCount=3 KnotsCount=2 Degree=2 IsPeriodic=0
    g1: ArcOfCircle CenterX=73.1223 CenterY=-32.291 CenterZ=0 NormalX=0 NormalY=0 NormalZ=1 AngleXU=0 Radius=13 StartAngle=5.92268 EndAngle=9.06428
    g2: ArcOfCircle CenterX=66.7816 CenterY=-49.1439 CenterZ=0 NormalX=0 NormalY=0 NormalZ=1 AngleXU=0 Radius=13 StartAngle=2.78068 EndAngle=5.92131
    g3: ArcOfCircle CenterX=55.9263 CenterY=-78.1807 CenterZ=0 NormalX=0 NormalY=0 NormalZ=1 AngleXU=0 Radius=13 StartAngle=5.92268 EndAngle=9.06428
    g4: ArcOfCircle CenterX=49.5884 CenterY=-95.0342 CenterZ=0 NormalX=0 NormalY=0 NormalZ=1 AngleXU=0 Radius=13 StartAngle=2.78068 EndAngle=5.92131
    g5: ArcOfCircle CenterX=38.7206 CenterY=-124.067 CenterZ=0 NormalX=0 NormalY=0 NormalZ=1 AngleXU=0 Radius=13 StartAngle=5.92268 EndAngle=9.06428
    g6: ArcOfCircle CenterX=32.3875 CenterY=-140.92 CenterZ=0 NormalX=0 NormalY=0 NormalZ=1 AngleXU=0 Radius=13 StartAngle=2.78068 EndAngle=5.92131
    g7: ArcOfCircle CenterX=21.4715 CenterY=-169.934 CenterZ=0 NormalX=0 NormalY=0 NormalZ=1 AngleXU=0 Radius=13 StartAngle=5.92268 EndAngle=9.06428
    g8: ArcOfCircle CenterX=15.1336 CenterY=-186.787 CenterZ=0 NormalX=0 NormalY=0 NormalZ=1 AngleXU=0 Radius=13 StartAngle=2.78068 EndAngle=5.92131
    g9-g12: Circle x4 (B-spline internal-alignment scaffolding for g13; pole/knot coordinates omitted)
    g13: BSplineCurve PolesCount=4 KnotsCount=2 Degree=3 IsPeriodic=0
    g14: GeomPoint X=28.8094 Y=-19.0875 Z=0
    g15: GeomPoint X=47.0443 Y=-50.4712 Z=0
    g16: Circle CenterX=53.5586 CenterY=-23.2695 CenterZ=0 NormalX=0 NormalY=0 NormalZ=1 AngleXU=0 Radius=3.24518
    g17: Circle CenterX=-195.441 CenterY=-127.082 CenterZ=0 NormalX=0 NormalY=0 NormalZ=1 AngleXU=0 Radius=1
    g18: Circle CenterX=-8.24091 CenterY=-197.481 CenterZ=0 NormalX=0 NormalY=0 NormalZ=1 AngleXU=0 Radius=1
    g19: Circle CenterX=12.8789 CenterY=-141.321 CenterZ=0 NormalX=0 NormalY=0 NormalZ=1 AngleXU=0 Radius=1
    g20: BSplineCurve PolesCount=3 KnotsCount=2 Degree=2 IsPeriodic=0
    g21: GeomPoint X=-195.441 Y=-127.082 Z=0
    g22: GeomPoint X=12.8789 Y=-141.321 Z=0
    g23: Circle CenterX=-12.8016 CenterY=-179.036 CenterZ=0 NormalX=0 NormalY=0 NormalZ=1 AngleXU=0 Radius=10.5072
    g24: Circle CenterX=0.933922 CenterY=-166.43 CenterZ=0 NormalX=0 NormalY=0 NormalZ=1 AngleXU=0 Radius=3.26661
    g25: Circle CenterX=-33.5518 CenterY=-176.44 CenterZ=0 NormalX=0 NormalY=0 NormalZ=1 AngleXU=0 Radius=5.64388
    g26: Circle CenterX=-47.2366 CenterY=-173.859 CenterZ=0 NormalX=0 NormalY=0 NormalZ=1 AngleXU=0 Radius=3.01653
    g27: Circle CenterX=-56.2595 CenterY=-171.456 CenterZ=0 NormalX=0 NormalY=0 NormalZ=1 AngleXU=0 Radius=2.12826
    g28: ArcOfCircle CenterX=51.2151 CenterY=-198.473 CenterZ=0 NormalX=0 NormalY=0 NormalZ=1 AngleXU=0 Radius=20 StartAngle=2.78189 EndAngle=4.35269
    g29: LineSegment StartX=32.4951 StartY=-191.433 StartZ=0 EndX=94.6578 EndY=-26.1352 EndZ=0
    g30: LineSegment StartX=43.1192 StartY=-220.001 StartZ=0 EndX=-196.497 EndY=-129.89 EndZ=0
    g31: LineSegment StartX=43.1192 StartY=-220.001 StartZ=0 EndX=44.1752 EndY=-217.193 EndZ=0
    g32: LineSegment StartX=117.223 StartY=-19.0875 StartZ=0 EndX=117.223 EndY=-16.0875 EndZ=0
    g33: LineSegment StartX=117.223 StartY=-16.0875 StartZ=0 EndX=17.2232 EndY=-16.0875 EndZ=0
    g34: LineSegment StartX=17.2232 StartY=-16.0875 StartZ=0 EndX=17.2232 EndY=-19.0875 EndZ=0
    g35: LineSegment StartX=28.8094 StartY=-19.0875 StartZ=0 EndX=17.2232 EndY=-19.0875 EndZ=0
    g36: LineSegment StartX=47.0443 StartY=-50.4712 StartZ=0 EndX=12.8789 EndY=-141.321 EndZ=0
    g37: LineSegment StartX=-195.441 StartY=-127.082 StartZ=0 EndX=-196.497 EndY=-129.89 EndZ=0
    g38: LineSegment StartX=85.2866 StartY=-36.8766 StartZ=0 EndX=78.9396 EndY=-53.7463 EndZ=0
    g39: LineSegment StartX=60.9579 StartY=-27.7053 StartZ=0 EndX=54.6191 EndY=-44.5532 EndZ=0
    g40: LineSegment StartX=68.0907 StartY=-82.7664 StartZ=0 EndX=61.7465 EndY=-99.6365 EndZ=0
    g41: LineSegment StartX=43.7619 StartY=-73.595 StartZ=0 EndX=37.426 EndY=-90.4435 EndZ=0
    g42: LineSegment StartX=50.885 StartY=-128.652 StartZ=0 EndX=44.5456 EndY=-145.522 EndZ=0
    g43: LineSegment StartX=26.5562 StartY=-119.481 StartZ=0 EndX=20.2251 EndY=-136.329 EndZ=0
    g44: LineSegment StartX=9.3071 StartY=-165.349 StartZ=0 EndX=2.97115 EndY=-182.197 EndZ=0
    g45: LineSegment StartX=33.6358 StartY=-174.52 StartZ=0 EndX=27.2917 EndY=-191.39 EndZ=0
  constraints (71):
    c: Block(g0)
    c: Block(g1)
    c: Block(g2)
    c: Block(g4)
    c: Block(g3)
    c: Block(g6)
    c: Block(g5)
    c: Block(g8)
    c: Block(g7)
    c: Weight(g9) = 1
    c: Equal(g9,g10)
    c: Equal(g9,g11)
    c: Equal(g9,g12)
    c: InternalAlignment(g9-g12 -> g13) x4
    c: InternalAlignment(g14,g13)
    c: InternalAlignment(g15,g13)
    c: Block(g16)
    c: Weight(g17) = 1
    c: Equal(g17,g18)
    c: Equal(g17,g19)
    c: InternalAlignment(g17,g20)
    c: InternalAlignment(g18,g20)
    c: InternalAlignment(g19,g20)
    c: InternalAlignment(g21,g20)
    c: InternalAlignment(g22,g20)
    c: Block(g20)
    c: Block(g23)
    c: Block(g24)
    c: Block(g25)
    c: Block(g26)
    c: Block(g27)
    c: Block(g28)
    c: Coincident(g29,g28)
    c: Coincident(g29,g0)
    c: Block(g13)
    c: Coincident(g31,g30)
    c: Coincident(g31,g28)
    c: Block(g31)
    c: Coincident(g32,g0)
    c: Vertical(g32)
    c: Coincident(g33,g32)
    c: Horizontal(g33)
    c: Coincident(g34,g33)
    c: Vertical(g34)
    c: Block(g33)
    c: Coincident(g35,g13)
    c: Coincident(g35,g34)
    c: Horizontal(g35)
    c: Coincident(g36,g13)
    c: Coincident(g36,g20)
    c: Coincident(g37,g20)
    c: Coincident(g37,g30)
    c: Block(g30)
    c: Coincident(g38,g1)
    c: Coincident(g38,g2)
    c: Coincident(g39,g1)
    c: Coincident(g39,g2)
    c: Coincident(g40,g3)
    c: Coincident(g40,g4)
    c: Coincident(g41,g3)
    c: Coincident(g41,g4)
    c: Coincident(g42,g5)
    c: Coincident(g42,g6)
    c: Coincident(g43,g5)
    c: Coincident(g43,g6)
    c: Coincident(g44,g7)
    c: Coincident(g44,g8)
    c: Coincident(g45,g7)
    c: Coincident(g45,g8)
    c: Distance(g30) = 256
    c: Distance(g33) = 100
FEATURE [Part::Extrusion] Extrude002
  Base = -> Sketch001
  Dir = (1,0,0)
  DirMode = 2
  FaceMakerClass = Part::FaceMakerBullseye
  LengthFwd = 8
  LengthRev = 0
  Solid = true
  Symmetric = false
FEATURE [Sketcher::SketchObject] Sketch002
  FullyConstrained = true
  sketch-geometry (20):
    g0: LineSegment StartX=-2.77179 StartY=-200.304 StartZ=0 EndX=5.22821 EndY=-200.304 EndZ=0
    g1: LineSegment StartX=5.22821 StartY=-200.304 StartZ=0 EndX=5.22821 EndY=-197.304 EndZ=0
    g2: LineSegment StartX=-2.77179 StartY=-200.304 StartZ=0 EndX=-2.77179 EndY=-197.304 EndZ=0
    g3: LineSegment StartX=5.22821 StartY=-197.304 StartZ=0 EndX=8.22821 EndY=-197.304 EndZ=0
    g4: LineSegment StartX=-2.77179 StartY=-197.304 StartZ=0 EndX=-5.77179 EndY=-197.304 EndZ=0
    g5: LineSegment StartX=19.2282 StartY=-203.304 StartZ=0 EndX=19.2282 EndY=-206.304 EndZ=0
    g6: LineSegment StartX=-16.7718 StartY=-203.304 StartZ=0 EndX=-16.7718 EndY=-206.304 EndZ=0
    g7: LineSegment StartX=-16.7718 StartY=-206.304 StartZ=0 EndX=19.2282 EndY=-206.304 EndZ=0
    g8: Circle CenterX=-16.7718 CenterY=-203.304 CenterZ=0 NormalX=0 NormalY=0 NormalZ=1 AngleXU=0 Radius=1
    g9: Circle CenterX=-5.77179 CenterY=-203.304 CenterZ=0 NormalX=0 NormalY=0 NormalZ=1 AngleXU=0 Radius=1
    g10: Circle CenterX=-5.77179 CenterY=-197.304 CenterZ=0 NormalX=0 NormalY=0 NormalZ=1 AngleXU=0 Radius=1
    g11: BSplineCurve PolesCount=3 KnotsCount=2 Degree=2 IsPeriodic=0
    g12: GeomPoint X=-16.7718 Y=-203.304 Z=0
    g13: GeomPoint X=-5.77179 Y=-197.304 Z=0
    g14: Circle CenterX=19.2282 CenterY=-203.304 CenterZ=0 NormalX=0 NormalY=0 NormalZ=1 AngleXU=0 Radius=1
    g15: Circle CenterX=8.22821 CenterY=-203.304 CenterZ=0 NormalX=0 NormalY=0 NormalZ=1 AngleXU=0 Radius=1
    g16: Circle CenterX=8.22821 CenterY=-197.304 CenterZ=0 NormalX=0 NormalY=0 NormalZ=1 AngleXU=0 Radius=1
    g17: BSplineCurve PolesCount=3 KnotsCount=2 Degree=2 IsPeriodic=0
    g18: GeomPoint X=19.2282 Y=-203.304 Z=0
    g19: GeomPoint X=8.22821 Y=-197.304 Z=0
  constraints (41):
    c: Horizontal(g0)
    c: Distance(g0) = 8
    c: Coincident(g1,g0)
    c: Vertical(g1)
    c: Distance(g1) = 3
    c: Coincident(g2,g0)
    c: Vertical(g2)
    c: Distance(g2) = 3
    c: Coincident(g3,g1)
    c: Horizontal(g3)
    c: Distance(g3) = 3
    c: Coincident(g4,g2)
    c: Horizontal(g4)
    c: Distance(g4) = 3
    c: Vertical(g5)
    c: Vertical(g6)
    c: Coincident(g7,g6)
    c: Coincident(g7,g5)
    c: Weight(g8) = 1
    c: Equal(g8,g9)
    c: Equal(g8,g10)
    c: Coincident(g11,g4)
    c: InternalAlignment(g8,g11)
    c: InternalAlignment(g9,g11)
    c: InternalAlignment(g10,g11)
    c: InternalAlignment(g12,g11)
    c: InternalAlignment(g13,g11)
    c: Coincident(g17,g5)
    c: Weight(g14) = 1
    c: Equal(g14,g15)
    c: Equal(g14,g16)
    c: Coincident(g17,g3)
    c: InternalAlignment(g14,g17)
    c: InternalAlignment(g15,g17)
    c: InternalAlignment(g16,g17)
    c: InternalAlignment(g18,g17)
    c: InternalAlignment(g19,g17)
    c: Block(g7)
    c: Block(g17)
    c: Block(g11)
    c: Block(g6)
FEATURE [Part::Extrusion] Extrude003
  Base = -> Sketch002
  Dir = (0,0,1)
  DirMode = 2
  FaceMakerClass = Part::FaceMakerBullseye
  LengthFwd = 260
  LengthRev = 0
  Solid = true
  Symmetric = false
FEATURE [Part::Extrusion] Extrude
  Base = -> Sketch
  Dir = (0,0,1)
  DirMode = 2
  FaceMakerClass = Part::FaceMakerBullseye
  LengthFwd = 14
  LengthRev = 0
  Solid = true
  Symmetric = false
